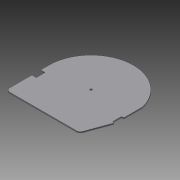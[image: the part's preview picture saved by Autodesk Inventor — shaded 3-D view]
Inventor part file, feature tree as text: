
AUTODESK INVENTOR PART (.ipt)
format: ipt  version: 2015 (Build 190159000, 159)  size: 120,320 bytes
history: native  units: mm
features: fillet x3, extrude x1, sketch x1
ambient origin geometry x8: Origin, YZ Plane, XZ Plane, XY Plane, X Axis, Y Axis, Z Axis, Center Point
bodies: Solid1 (feature_tree)
feature tree (5):
  extrude  "Extrusion1"  Depth=57.0mm
  fillet  "Fillet1"  Radius=20.0mm
  fillet  "Fillet2"  Radius=6.0mm
  fillet  "Fillet3"  Radius=12.0mm
  sketch  "Sketch1"  dims[d0=3.0mm d1=57.0mm d2=20.0mm d3=6.0mm d4=12.0mm d5=55.0mm d6=3.0mm d7=19.198622mm d8=99.0mm d9=47.0mm d10=58.0mm d11=1.5mm d12=0.0mm d13=0.5mm d14=1.0mm d15=5.0mm]
